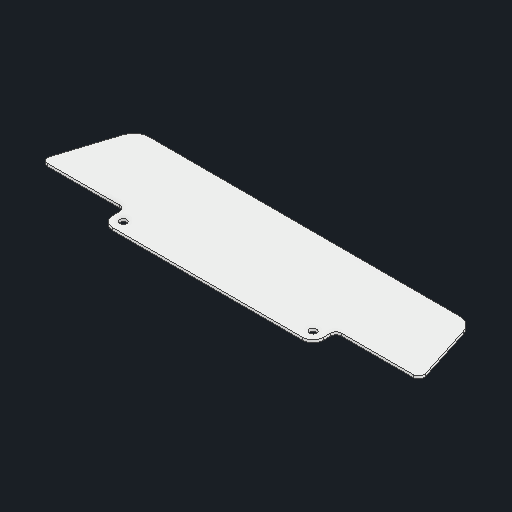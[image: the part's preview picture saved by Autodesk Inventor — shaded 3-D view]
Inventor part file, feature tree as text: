
AUTODESK INVENTOR PART (.ipt)
format: ipt  version: 2025 (Build 290162000, 162)  size: 157,696 bytes
history: native  units: in
note: dims shown in document units (in); Inventor stores cm internally (conversion verified against a paired STEP export)
features: other x6, sketch x1, extrude x1
ambient origin geometry x8: Origin, YZ Plane, XZ Plane, XY Plane, X Axis, Y Axis, Z Axis, Center Point
bodies: Solid1 (feature_tree)
feature tree (8):
  other  "Blocks"
  sketch  "Sketch1"  dims[d0=0.5in d7=0.0625in d8=0.0in d11=2.0in d17=0.375in d18=0.375in d19=0.125in d20=0.125in d21=0.125in d22=60.0deg d23=1.75in d24=0.172in d25=7.3527in d26=0.125in]
  extrude  "Extrusion1"  Depth=0.0625in TaperAngle=0.0deg
  other  "Bend Part2"
  other  "A-Side Definition"
  other  "main"
  other  "main:1"
  other  "Definition1"
